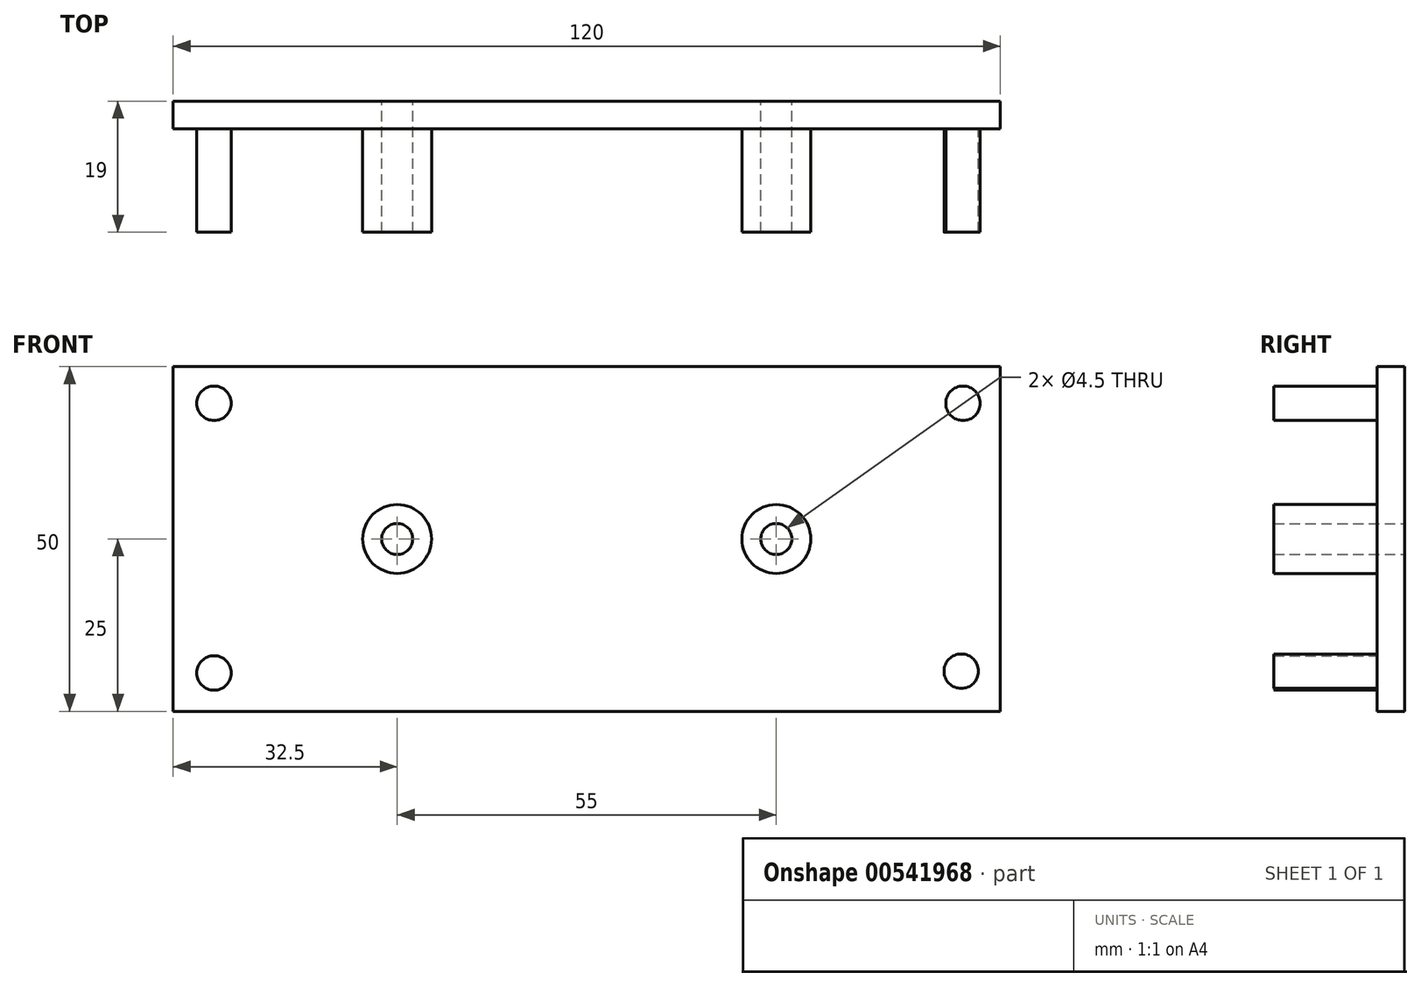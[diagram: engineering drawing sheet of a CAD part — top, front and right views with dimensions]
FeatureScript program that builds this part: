
annotation { "Feature Type Name" : "Feature", "Feature Type Description" : "" }
export const myFeature = defineFeature(function(context is Context, id is Id, definition is map)
    precondition{}
    {
        {
            var Q0;
            Q0=qCreatedBy(makeId("Front.planeOp"),FACE);
            var sketch = newSketch(context, id + "F0", { "sketchPlane" : qUnion([Q0])});
            skLineSegment(sketch, "E0", {"start": v(0, -25) * mm, "end": v(-60, -25) * mm});
            skLineSegment(sketch, "E1", {"start": v(0, -25) * mm, "end": v(60, -25) * mm});
            skLineSegment(sketch, "E2", {"start": v(60, -25) * mm, "end": v(60, 25) * mm});
            skLineSegment(sketch, "E3", {"start": v(60, 25) * mm, "end": v(-60, 25) * mm});
            skLineSegment(sketch, "E4", {"start": v(-60, 25) * mm, "end": v(-60, -25) * mm});
            skCircle(sketch, "E5", {"center": v(-27.5, 0) * mm, "radius": 2.25 * mm});
            skCircle(sketch, "E6", {"center": v(27.5, 0) * mm, "radius": 2.25 * mm});
            skSolve(sketch);
        }
        {
            var Q0;
            Q0=makeQuery(id+"F0.imprint","IMPRINT",FACE,{"disambiguationData":[TD([[makeQuery(id+"F0.imprint","IMPRINT",EDGE,{"derivedFrom":sQuery(id+"F0.wireOp",EDGE,"E0")}),-1.0]])]});
            extrude(context, id + "F1", {"entities" : qUnion([Q0]), "depth" : 4 * mm, "offsetDistance" : 25 * mm});
        }
        {
            var Q0;
            Q0=makeQuery(id+"F1.opExtrude","CAP_FACE",FACE,{"disambiguationData":[OSD([sQuery(id+"F0.wireOp",EDGE,"E0"),sQuery(id+"F0.wireOp",EDGE,"E1"),sQuery(id+"F0.wireOp",EDGE,"E2"),sQuery(id+"F0.wireOp",EDGE,"E3"),sQuery(id+"F0.wireOp",EDGE,"E4"),sQuery(id+"F0.wireOp",EDGE,"E5"),sQuery(id+"F0.wireOp",EDGE,"E6")])],"isStart":false});
            var sketch = newSketch(context, id + "F2", { "sketchPlane" : qUnion([Q0])});
            skCircle(sketch, "E7", {"center": v(-27.5, 0) * mm, "radius": 5 * mm});
            skCircle(sketch, "E8", {"center": v(27.5, 0) * mm, "radius": 5 * mm});
            skSolve(sketch);
        }
        {
            var Q0;
            Q0=makeQuery(id+"F2.imprint","IMPRINT",FACE,{"disambiguationData":[TD([[makeQuery(id+"F2.imprint","IMPRINT",EDGE,{"derivedFrom":sQuery(id+"F2.wireOp",EDGE,"E7")}),1.0]])]});
            var Q1;
            Q1=makeQuery(id+"F2.imprint","IMPRINT",FACE,{"disambiguationData":[TD([[makeQuery(id+"F2.imprint","IMPRINT",EDGE,{"derivedFrom":sQuery(id+"F2.wireOp",EDGE,"E8")}),1.0]])]});
            extrude(context, id + "F3", {"entities" : qUnion([Q0, Q1]), "operationType" : NewBodyOperationType.ADD, "depth" : 15 * mm, "offsetDistance" : 25 * mm});
        }
        {
            var Q0;
            Q0=makeQuery(id+"F1.opExtrude","CAP_FACE",FACE,{"disambiguationData":[OSD([sQuery(id+"F0.wireOp",EDGE,"E0"),sQuery(id+"F0.wireOp",EDGE,"E1"),sQuery(id+"F0.wireOp",EDGE,"E2"),sQuery(id+"F0.wireOp",EDGE,"E3"),sQuery(id+"F0.wireOp",EDGE,"E4"),sQuery(id+"F0.wireOp",EDGE,"E5"),sQuery(id+"F0.wireOp",EDGE,"E6")])],"isStart":false});
            var sketch = newSketch(context, id + "F4", { "sketchPlane" : qUnion([Q0])});
            skCircle(sketch, "E9", {"center": v(-54.08, 19.69) * mm, "radius": 2.5 * mm});
            skCircle(sketch, "E10", {"center": v(54.59, 19.69) * mm, "radius": 2.5 * mm});
            skCircle(sketch, "E11", {"center": v(54.33, -19.18) * mm, "radius": 2.5 * mm});
            skCircle(sketch, "E12", {"center": v(-54.08, -19.43) * mm, "radius": 2.5 * mm});
            skSolve(sketch);
        }
        {
            var Q0;
            Q0=makeQuery(id+"F4.imprint","IMPRINT",FACE,{"disambiguationData":[TD([[makeQuery(id+"F4.imprint","IMPRINT",EDGE,{"derivedFrom":sQuery(id+"F4.wireOp",EDGE,"E9")}),1.0]])]});
            var Q1;
            Q1=makeQuery(id+"F4.imprint","IMPRINT",FACE,{"disambiguationData":[TD([[makeQuery(id+"F4.imprint","IMPRINT",EDGE,{"derivedFrom":sQuery(id+"F4.wireOp",EDGE,"E12")}),1.0]])]});
            var Q2;
            Q2=makeQuery(id+"F4.imprint","IMPRINT",FACE,{"disambiguationData":[TD([[makeQuery(id+"F4.imprint","IMPRINT",EDGE,{"derivedFrom":sQuery(id+"F4.wireOp",EDGE,"E11")}),1.0]])]});
            var Q3;
            Q3=makeQuery(id+"F4.imprint","IMPRINT",FACE,{"disambiguationData":[TD([[makeQuery(id+"F4.imprint","IMPRINT",EDGE,{"derivedFrom":sQuery(id+"F4.wireOp",EDGE,"E10")}),1.0]])]});
            extrude(context, id + "F5", {"entities" : qUnion([Q0, Q1, Q2, Q3]), "operationType" : NewBodyOperationType.ADD, "depth" : 15 * mm, "offsetDistance" : 25 * mm});
        }
    });
